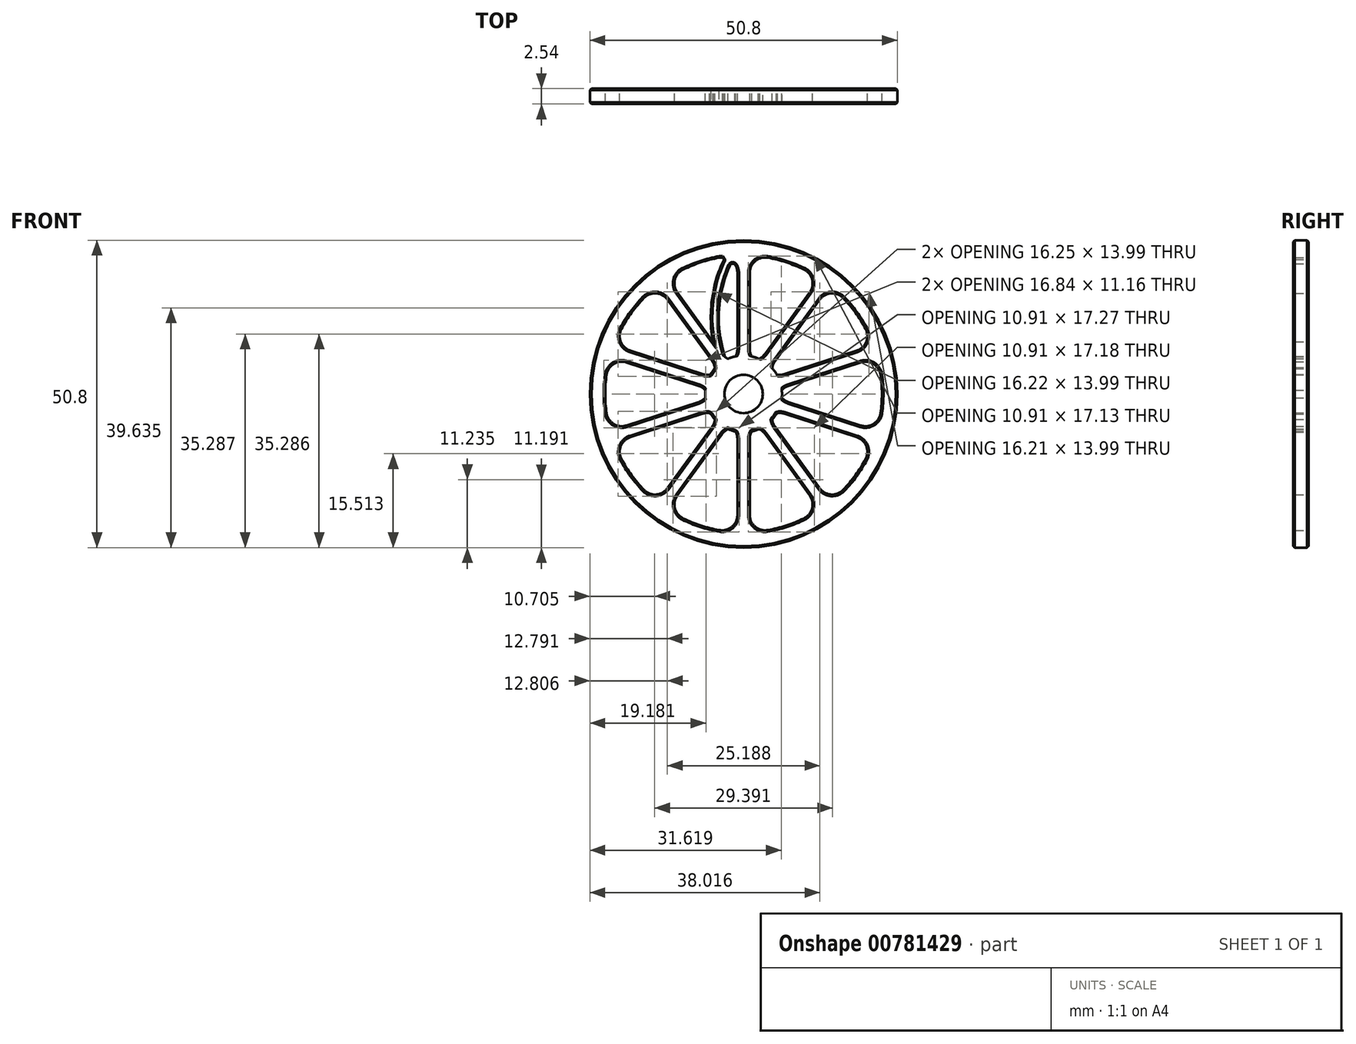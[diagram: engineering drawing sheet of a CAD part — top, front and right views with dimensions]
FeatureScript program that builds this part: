
annotation { "Feature Type Name" : "Feature", "Feature Type Description" : "" }
export const myFeature = defineFeature(function(context is Context, id is Id, definition is map)
    precondition{}
    {
        {
            var Q0;
            Q0=qCreatedBy(makeId("Front.planeOp"),FACE);
            var sketch = newSketch(context, id + "F0", { "sketchPlane" : qUnion([Q0])});
            skCircle(sketch, "E0", {"center": v(0, 0) * mm, "radius": 25.4 * mm});
            skCircle(sketch, "E1", {"center": v(0, 0) * mm, "radius": 3.18 * mm});
            skArc(sketch, "E2", {"start": v(-4, 22.5) * mm, "mid": v(-7.06, 21.74) * mm, "end": v(-10, 20.56) * mm});
            skLineSegment(sketch, "E3", {"start": v(-1.02, 7.45) * mm, "end": v(-1.02, 20) * mm});
            skLineSegment(sketch, "E4.MirrorCS", {"start": v(1.02, 7.45) * mm, "end": v(1.02, 20) * mm});
            skPoint(sketch, "E5.visualSharp", {"position": v(-1.02, 5.62) * mm});
            skArc(sketch, "E5.filletArc", {"start": v(-1.34, 6.2) * mm, "mid": v(-1.1, 6.8) * mm, "end": v(-1.02, 7.45) * mm});
            skPoint(sketch, "E6.visualSharp", {"position": v(1.02, 5.62) * mm});
            skArc(sketch, "E6.filletArc", {"start": v(1.02, 7.45) * mm, "mid": v(1.1, 6.8) * mm, "end": v(1.34, 6.2) * mm});
            skPoint(sketch, "E7.visualSharp", {"position": v(1.02, 22.84) * mm});
            skArc(sketch, "E7.filletArc", {"start": v(4, 22.5) * mm, "mid": v(1.92, 21.95) * mm, "end": v(1.02, 20) * mm});
            skPoint(sketch, "E8.visualSharp", {"position": v(-1.02, 22.84) * mm});
            skArc(sketch, "E8.filletArc", {"start": v(-1.02, 20) * mm, "mid": v(-1.92, 21.95) * mm, "end": v(-4, 22.5) * mm});
            skLineSegment(sketch, "E9.1.0", {"start": v(-5.2, 5.43) * mm, "end": v(-12.58, 15.59) * mm});
            skArc(sketch, "E9.1.1", {"start": v(-12.58, 15.59) * mm, "mid": v(-14.46, 16.63) * mm, "end": v(-16.47, 15.86) * mm});
            skArc(sketch, "E9.1.2", {"start": v(-10, 20.56) * mm, "mid": v(-11.35, 18.9) * mm, "end": v(-10.94, 16.78) * mm});
            skLineSegment(sketch, "E9.1.3", {"start": v(-3.56, 6.62) * mm, "end": v(-10.94, 16.78) * mm});
            skArc(sketch, "E9.1.4", {"start": v(-3.56, 6.62) * mm, "mid": v(-3.11, 6.15) * mm, "end": v(-2.56, 5.8) * mm});
            skArc(sketch, "E9.1.5", {"start": v(-4.73, 4.23) * mm, "mid": v(-4.9, 4.86) * mm, "end": v(-5.2, 5.43) * mm});
            skLineSegment(sketch, "E9.2.0", {"start": v(-7.4, 1.34) * mm, "end": v(-19.34, 5.22) * mm});
            skArc(sketch, "E9.2.1", {"start": v(-19.34, 5.22) * mm, "mid": v(-21.47, 4.95) * mm, "end": v(-22.64, 3.15) * mm});
            skArc(sketch, "E9.2.2", {"start": v(-20.17, 10.76) * mm, "mid": v(-20.28, 8.61) * mm, "end": v(-18.71, 7.15) * mm});
            skLineSegment(sketch, "E9.2.3", {"start": v(-6.77, 3.27) * mm, "end": v(-18.71, 7.15) * mm});
            skArc(sketch, "E9.2.4", {"start": v(-6.77, 3.27) * mm, "mid": v(-6.13, 3.15) * mm, "end": v(-5.49, 3.2) * mm});
            skArc(sketch, "E9.2.5", {"start": v(-6.32, 0.64) * mm, "mid": v(-6.81, 1.06) * mm, "end": v(-7.4, 1.34) * mm});
            skLineSegment(sketch, "E9.3.0", {"start": v(-6.77, -3.27) * mm, "end": v(-18.71, -7.15) * mm});
            skArc(sketch, "E9.3.1", {"start": v(-18.71, -7.15) * mm, "mid": v(-20.28, -8.61) * mm, "end": v(-20.17, -10.76) * mm});
            skArc(sketch, "E9.3.2", {"start": v(-22.64, -3.15) * mm, "mid": v(-21.47, -4.95) * mm, "end": v(-19.34, -5.22) * mm});
            skLineSegment(sketch, "E9.3.3", {"start": v(-7.4, -1.34) * mm, "end": v(-19.34, -5.22) * mm});
            skArc(sketch, "E9.3.4", {"start": v(-7.4, -1.34) * mm, "mid": v(-6.81, -1.06) * mm, "end": v(-6.32, -0.64) * mm});
            skArc(sketch, "E9.3.5", {"start": v(-5.49, -3.2) * mm, "mid": v(-6.13, -3.15) * mm, "end": v(-6.77, -3.27) * mm});
            skLineSegment(sketch, "E9.4.0", {"start": v(-3.56, -6.62) * mm, "end": v(-10.94, -16.78) * mm});
            skArc(sketch, "E9.4.1", {"start": v(-10.94, -16.78) * mm, "mid": v(-11.35, -18.9) * mm, "end": v(-10, -20.56) * mm});
            skArc(sketch, "E9.4.2", {"start": v(-16.47, -15.86) * mm, "mid": v(-14.46, -16.63) * mm, "end": v(-12.58, -15.59) * mm});
            skLineSegment(sketch, "E9.4.3", {"start": v(-5.2, -5.43) * mm, "end": v(-12.58, -15.59) * mm});
            skArc(sketch, "E9.4.4", {"start": v(-5.2, -5.43) * mm, "mid": v(-4.9, -4.86) * mm, "end": v(-4.73, -4.23) * mm});
            skArc(sketch, "E9.4.5", {"start": v(-2.56, -5.8) * mm, "mid": v(-3.11, -6.15) * mm, "end": v(-3.56, -6.62) * mm});
            skLineSegment(sketch, "E9.5.0", {"start": v(1.02, -7.45) * mm, "end": v(1.02, -20) * mm});
            skArc(sketch, "E9.5.1", {"start": v(1.02, -20) * mm, "mid": v(1.92, -21.95) * mm, "end": v(4, -22.5) * mm});
            skArc(sketch, "E9.5.2", {"start": v(-4, -22.5) * mm, "mid": v(-1.92, -21.95) * mm, "end": v(-1.02, -20) * mm});
            skLineSegment(sketch, "E9.5.3", {"start": v(-1.02, -7.45) * mm, "end": v(-1.02, -20) * mm});
            skArc(sketch, "E9.5.4", {"start": v(-1.02, -7.45) * mm, "mid": v(-1.1, -6.8) * mm, "end": v(-1.34, -6.2) * mm});
            skArc(sketch, "E9.5.5", {"start": v(1.34, -6.2) * mm, "mid": v(1.1, -6.8) * mm, "end": v(1.02, -7.45) * mm});
            skLineSegment(sketch, "E9.6.0", {"start": v(5.2, -5.43) * mm, "end": v(12.58, -15.59) * mm});
            skArc(sketch, "E9.6.1", {"start": v(12.58, -15.59) * mm, "mid": v(14.46, -16.63) * mm, "end": v(16.47, -15.86) * mm});
            skArc(sketch, "E9.6.2", {"start": v(10, -20.56) * mm, "mid": v(11.35, -18.9) * mm, "end": v(10.94, -16.78) * mm});
            skLineSegment(sketch, "E9.6.3", {"start": v(3.56, -6.62) * mm, "end": v(10.94, -16.78) * mm});
            skArc(sketch, "E9.6.4", {"start": v(3.56, -6.62) * mm, "mid": v(3.11, -6.15) * mm, "end": v(2.56, -5.8) * mm});
            skArc(sketch, "E9.6.5", {"start": v(4.73, -4.23) * mm, "mid": v(4.9, -4.86) * mm, "end": v(5.2, -5.43) * mm});
            skLineSegment(sketch, "E9.7.0", {"start": v(7.4, -1.34) * mm, "end": v(19.34, -5.22) * mm});
            skArc(sketch, "E9.7.1", {"start": v(19.34, -5.22) * mm, "mid": v(21.47, -4.95) * mm, "end": v(22.64, -3.15) * mm});
            skArc(sketch, "E9.7.2", {"start": v(20.17, -10.76) * mm, "mid": v(20.28, -8.61) * mm, "end": v(18.71, -7.15) * mm});
            skLineSegment(sketch, "E9.7.3", {"start": v(6.77, -3.27) * mm, "end": v(18.71, -7.15) * mm});
            skArc(sketch, "E9.7.4", {"start": v(6.77, -3.27) * mm, "mid": v(6.13, -3.15) * mm, "end": v(5.49, -3.2) * mm});
            skArc(sketch, "E9.7.5", {"start": v(6.32, -0.64) * mm, "mid": v(6.81, -1.06) * mm, "end": v(7.4, -1.34) * mm});
            skLineSegment(sketch, "E9.8.0", {"start": v(6.77, 3.27) * mm, "end": v(18.71, 7.15) * mm});
            skArc(sketch, "E9.8.1", {"start": v(18.71, 7.15) * mm, "mid": v(20.28, 8.61) * mm, "end": v(20.17, 10.76) * mm});
            skArc(sketch, "E9.8.2", {"start": v(22.64, 3.15) * mm, "mid": v(21.47, 4.95) * mm, "end": v(19.34, 5.22) * mm});
            skLineSegment(sketch, "E9.8.3", {"start": v(7.4, 1.34) * mm, "end": v(19.34, 5.22) * mm});
            skArc(sketch, "E9.8.4", {"start": v(7.4, 1.34) * mm, "mid": v(6.81, 1.06) * mm, "end": v(6.32, 0.64) * mm});
            skArc(sketch, "E9.8.5", {"start": v(5.49, 3.2) * mm, "mid": v(6.13, 3.15) * mm, "end": v(6.77, 3.27) * mm});
            skLineSegment(sketch, "E9.9.0", {"start": v(3.56, 6.62) * mm, "end": v(10.94, 16.78) * mm});
            skArc(sketch, "E9.9.1", {"start": v(10.94, 16.78) * mm, "mid": v(11.35, 18.9) * mm, "end": v(10, 20.56) * mm});
            skArc(sketch, "E9.9.2", {"start": v(16.47, 15.86) * mm, "mid": v(14.46, 16.63) * mm, "end": v(12.58, 15.59) * mm});
            skLineSegment(sketch, "E9.9.3", {"start": v(5.2, 5.43) * mm, "end": v(12.58, 15.59) * mm});
            skArc(sketch, "E9.9.4", {"start": v(5.2, 5.43) * mm, "mid": v(4.9, 4.86) * mm, "end": v(4.73, 4.23) * mm});
            skArc(sketch, "E9.9.5", {"start": v(2.56, 5.8) * mm, "mid": v(3.11, 6.15) * mm, "end": v(3.56, 6.62) * mm});
            skArc(sketch, "E10.trimOffspring", {"start": v(-16.47, 15.86) * mm, "mid": v(-18.5, 13.44) * mm, "end": v(-20.17, 10.76) * mm});
            skArc(sketch, "E11.trimOffspring", {"start": v(10, 20.56) * mm, "mid": v(7.06, 21.74) * mm, "end": v(4, 22.5) * mm});
            skArc(sketch, "E12.trimOffspring", {"start": v(20.17, 10.76) * mm, "mid": v(18.5, 13.44) * mm, "end": v(16.47, 15.86) * mm});
            skArc(sketch, "E13.trimOffspring", {"start": v(22.64, -3.15) * mm, "mid": v(22.86, 0) * mm, "end": v(22.64, 3.15) * mm});
            skArc(sketch, "E14.trimOffspring", {"start": v(16.47, -15.86) * mm, "mid": v(18.5, -13.44) * mm, "end": v(20.17, -10.76) * mm});
            skArc(sketch, "E15.trimOffspring", {"start": v(4, -22.5) * mm, "mid": v(7.06, -21.74) * mm, "end": v(10, -20.56) * mm});
            skArc(sketch, "E16.trimOffspring", {"start": v(-10, -20.56) * mm, "mid": v(-7.06, -21.74) * mm, "end": v(-4, -22.5) * mm});
            skArc(sketch, "E17.trimOffspring", {"start": v(-20.17, -10.76) * mm, "mid": v(-18.5, -13.44) * mm, "end": v(-16.47, -15.86) * mm});
            skArc(sketch, "E18.trimOffspring", {"start": v(-22.64, 3.15) * mm, "mid": v(-22.86, 0) * mm, "end": v(-22.64, -3.15) * mm});
            skPoint(sketch, "E19.orphan", {"position": v(-5.67, 0.75) * mm});
            skPoint(sketch, "E20.orphan", {"position": v(-5.67, -0.75) * mm});
            skPoint(sketch, "E21.orphan", {"position": v(-4.14, 3.94) * mm});
            skPoint(sketch, "E22.orphan", {"position": v(-5.02, 2.73) * mm});
            skPoint(sketch, "E23.orphan", {"position": v(-1.04, 5.62) * mm});
            skPoint(sketch, "E24.orphan", {"position": v(1.04, 5.62) * mm});
            skPoint(sketch, "E25.orphan", {"position": v(4.14, 3.94) * mm});
            skPoint(sketch, "E26.orphan", {"position": v(5.02, 2.73) * mm});
            skPoint(sketch, "E27.orphan", {"position": v(5.67, 0.75) * mm});
            skPoint(sketch, "E28.orphan", {"position": v(5.67, -0.75) * mm});
            skPoint(sketch, "E29.orphan", {"position": v(5.02, -2.73) * mm});
            skPoint(sketch, "E30.orphan", {"position": v(4.14, -3.94) * mm});
            skPoint(sketch, "E31.orphan", {"position": v(2.46, -5.16) * mm});
            skPoint(sketch, "E32.orphan", {"position": v(1.04, -5.62) * mm});
            skPoint(sketch, "E33.orphan", {"position": v(-1.04, -5.62) * mm});
            skPoint(sketch, "E34.orphan", {"position": v(-2.46, -5.16) * mm});
            skPoint(sketch, "E35.orphan", {"position": v(-4.14, -3.94) * mm});
            skPoint(sketch, "E36.orphan", {"position": v(-5.02, -2.73) * mm});
            skPoint(sketch, "E37.orphan", {"position": v(-2.46, 5.16) * mm});
            skArc(sketch, "E38", {"start": v(-4.73, 4.23) * mm, "mid": v(-5.14, 3.73) * mm, "end": v(-5.49, 3.2) * mm});
            skArc(sketch, "E39.trimOffspring", {"start": v(-1.34, 6.2) * mm, "mid": v(-1.96, 6.04) * mm, "end": v(-2.56, 5.8) * mm});
            skArc(sketch, "E40.trimOffspring", {"start": v(2.56, 5.8) * mm, "mid": v(1.96, 6.04) * mm, "end": v(1.34, 6.2) * mm});
            skArc(sketch, "E41.trimOffspring", {"start": v(5.49, 3.2) * mm, "mid": v(5.14, 3.73) * mm, "end": v(4.73, 4.23) * mm});
            skArc(sketch, "E42.trimOffspring", {"start": v(6.32, -0.64) * mm, "mid": v(6.35, 0) * mm, "end": v(6.32, 0.64) * mm});
            skArc(sketch, "E43.trimOffspring", {"start": v(-6.32, 0.64) * mm, "mid": v(-6.35, 0) * mm, "end": v(-6.32, -0.64) * mm});
            skArc(sketch, "E44.trimOffspring", {"start": v(-5.49, -3.2) * mm, "mid": v(-5.14, -3.73) * mm, "end": v(-4.73, -4.23) * mm});
            skArc(sketch, "E45.trimOffspring", {"start": v(1.34, -6.2) * mm, "mid": v(1.96, -6.04) * mm, "end": v(2.56, -5.8) * mm});
            skArc(sketch, "E46.trimOffspring", {"start": v(4.73, -4.23) * mm, "mid": v(5.14, -3.73) * mm, "end": v(5.49, -3.2) * mm});
            skArc(sketch, "E47.trimOffspring", {"start": v(-2.56, -5.8) * mm, "mid": v(-1.96, -6.04) * mm, "end": v(-1.34, -6.2) * mm});
            skSolve(sketch);
        }
        {
            var Q0;
            Q0=makeQuery(id+"F0.imprint","IMPRINT",FACE,{"disambiguationData":[TD([[makeQuery(id+"F0.imprint","IMPRINT",EDGE,{"derivedFrom":sQuery(id+"F0.wireOp",EDGE,"E0")}),1.0]])]});
            extrude(context, id + "F1", {"entities" : qUnion([Q0]), "depth" : 2.54 * mm, "offsetDistance" : 25.4 * mm});
        }
        {
            var Q0;
            Q0=makeQuery(id+"F1.opExtrude","CAP_FACE",FACE,{"disambiguationData":[OSD([sQuery(id+"F0.wireOp",EDGE,"E0"),sQuery(id+"F0.wireOp",EDGE,"E1"),sQuery(id+"F0.wireOp",EDGE,"E2"),sQuery(id+"F0.wireOp",EDGE,"E3"),sQuery(id+"F0.wireOp",EDGE,"E4.MirrorCS"),sQuery(id+"F0.wireOp",EDGE,"E5.filletArc"),sQuery(id+"F0.wireOp",EDGE,"E6.filletArc"),sQuery(id+"F0.wireOp",EDGE,"E7.filletArc"),sQuery(id+"F0.wireOp",EDGE,"E8.filletArc"),sQuery(id+"F0.wireOp",EDGE,"E9.1.0"),sQuery(id+"F0.wireOp",EDGE,"E9.1.1"),sQuery(id+"F0.wireOp",EDGE,"E9.1.2"),sQuery(id+"F0.wireOp",EDGE,"E9.1.3"),sQuery(id+"F0.wireOp",EDGE,"E9.1.4"),sQuery(id+"F0.wireOp",EDGE,"E9.1.5"),sQuery(id+"F0.wireOp",EDGE,"E9.2.0"),sQuery(id+"F0.wireOp",EDGE,"E9.2.1"),sQuery(id+"F0.wireOp",EDGE,"E9.2.2"),sQuery(id+"F0.wireOp",EDGE,"E9.2.3"),sQuery(id+"F0.wireOp",EDGE,"E9.2.4"),sQuery(id+"F0.wireOp",EDGE,"E9.2.5"),sQuery(id+"F0.wireOp",EDGE,"E9.3.0"),sQuery(id+"F0.wireOp",EDGE,"E9.3.1"),sQuery(id+"F0.wireOp",EDGE,"E9.3.2"),sQuery(id+"F0.wireOp",EDGE,"E9.3.3"),sQuery(id+"F0.wireOp",EDGE,"E9.3.4"),sQuery(id+"F0.wireOp",EDGE,"E9.3.5"),sQuery(id+"F0.wireOp",EDGE,"E9.4.0"),sQuery(id+"F0.wireOp",EDGE,"E9.4.1"),sQuery(id+"F0.wireOp",EDGE,"E9.4.2"),sQuery(id+"F0.wireOp",EDGE,"E9.4.3"),sQuery(id+"F0.wireOp",EDGE,"E9.4.4"),sQuery(id+"F0.wireOp",EDGE,"E9.4.5"),sQuery(id+"F0.wireOp",EDGE,"E9.5.0"),sQuery(id+"F0.wireOp",EDGE,"E9.5.1"),sQuery(id+"F0.wireOp",EDGE,"E9.5.2"),sQuery(id+"F0.wireOp",EDGE,"E9.5.3"),sQuery(id+"F0.wireOp",EDGE,"E9.5.4"),sQuery(id+"F0.wireOp",EDGE,"E9.5.5"),sQuery(id+"F0.wireOp",EDGE,"E9.6.0"),sQuery(id+"F0.wireOp",EDGE,"E9.6.1"),sQuery(id+"F0.wireOp",EDGE,"E9.6.2"),sQuery(id+"F0.wireOp",EDGE,"E9.6.3"),sQuery(id+"F0.wireOp",EDGE,"E9.6.4"),sQuery(id+"F0.wireOp",EDGE,"E9.6.5"),sQuery(id+"F0.wireOp",EDGE,"E9.7.0"),sQuery(id+"F0.wireOp",EDGE,"E9.7.1"),sQuery(id+"F0.wireOp",EDGE,"E9.7.2"),sQuery(id+"F0.wireOp",EDGE,"E9.7.3"),sQuery(id+"F0.wireOp",EDGE,"E9.7.4"),sQuery(id+"F0.wireOp",EDGE,"E9.7.5"),sQuery(id+"F0.wireOp",EDGE,"E9.8.0"),sQuery(id+"F0.wireOp",EDGE,"E9.8.1"),sQuery(id+"F0.wireOp",EDGE,"E9.8.2"),sQuery(id+"F0.wireOp",EDGE,"E9.8.3"),sQuery(id+"F0.wireOp",EDGE,"E9.8.4"),sQuery(id+"F0.wireOp",EDGE,"E9.8.5"),sQuery(id+"F0.wireOp",EDGE,"E9.9.0"),sQuery(id+"F0.wireOp",EDGE,"E9.9.1"),sQuery(id+"F0.wireOp",EDGE,"E9.9.2"),sQuery(id+"F0.wireOp",EDGE,"E9.9.3"),sQuery(id+"F0.wireOp",EDGE,"E9.9.4"),sQuery(id+"F0.wireOp",EDGE,"E9.9.5"),sQuery(id+"F0.wireOp",EDGE,"E10.trimOffspring"),sQuery(id+"F0.wireOp",EDGE,"E11.trimOffspring"),sQuery(id+"F0.wireOp",EDGE,"E12.trimOffspring"),sQuery(id+"F0.wireOp",EDGE,"E13.trimOffspring"),sQuery(id+"F0.wireOp",EDGE,"E14.trimOffspring"),sQuery(id+"F0.wireOp",EDGE,"E15.trimOffspring"),sQuery(id+"F0.wireOp",EDGE,"E16.trimOffspring"),sQuery(id+"F0.wireOp",EDGE,"E17.trimOffspring"),sQuery(id+"F0.wireOp",EDGE,"E18.trimOffspring"),sQuery(id+"F0.wireOp",EDGE,"E44.trimOffspring"),sQuery(id+"F0.wireOp",EDGE,"E47.trimOffspring"),sQuery(id+"F0.wireOp",EDGE,"E45.trimOffspring"),sQuery(id+"F0.wireOp",EDGE,"E46.trimOffspring"),sQuery(id+"F0.wireOp",EDGE,"E42.trimOffspring"),sQuery(id+"F0.wireOp",EDGE,"E41.trimOffspring"),sQuery(id+"F0.wireOp",EDGE,"E40.trimOffspring"),sQuery(id+"F0.wireOp",EDGE,"E39.trimOffspring"),sQuery(id+"F0.wireOp",EDGE,"E38"),sQuery(id+"F0.wireOp",EDGE,"E43.trimOffspring")])],"isStart":true});
            var sketch = newSketch(context, id + "F2", { "sketchPlane" : qUnion([Q0])});
            skLineSegment(sketch, "E48", {"start": v(1.02, 13.73) * mm, "end": v(7.25, 11.7) * mm, "construction": true});
            skFitSpline(sketch, "E49", {"points": [v(1.92, 21.95) * mm, v(4.13, 12.72) * mm, v(3.11, 6.15) * mm], "startDerivative": vector(8, -16.77) * mm, "endDerivative": vector(-3.67, -13.83) * mm});
            skFitSpline(sketch, "E50.0", {"points": [v(3.07, 22.5) * mm, v(3.78, 21.02) * mm, v(4.59, 18.72) * mm, v(5.2, 15.68) * mm, v(5.38, 13.84) * mm, v(5.41, 12.42) * mm, v(5.36, 11.05) * mm, v(5.17, 9.42) * mm, v(4.8, 7.59) * mm, v(4.5, 6.41) * mm, v(4.34, 5.83) * mm]});
            skLineSegment(sketch, "E51.0", {"start": v(3.56, 6.62) * mm, "end": v(10.94, 16.78) * mm});
            skArc(sketch, "E52.0", {"start": v(3.56, 6.62) * mm, "mid": v(3.11, 6.15) * mm, "end": v(2.56, 5.8) * mm});
            skArc(sketch, "E53.0", {"start": v(1.02, 20) * mm, "mid": v(1.92, 21.95) * mm, "end": v(4, 22.5) * mm});
            skSolve(sketch);
        }
        {
            var Q0;
            {var subQ3=sQuery(id+"F2.wireOp",EDGE,"E49");Q0=makeQuery(id+"F2.imprint","IMPRINT",FACE,{"disambiguationData":[TD([[makeQuery(id+"F2.imprint","IMPRINT",EDGE,{"derivedFrom":subQ3}),1.0]])]});}
            var Q1;
            Q1=makeQuery(id+"F1.opExtrude","CAP_FACE",FACE,{"disambiguationData":[OSD([sQuery(id+"F0.wireOp",EDGE,"E0"),sQuery(id+"F0.wireOp",EDGE,"E1"),sQuery(id+"F0.wireOp",EDGE,"E2"),sQuery(id+"F0.wireOp",EDGE,"E3"),sQuery(id+"F0.wireOp",EDGE,"E4.MirrorCS"),sQuery(id+"F0.wireOp",EDGE,"E5.filletArc"),sQuery(id+"F0.wireOp",EDGE,"E6.filletArc"),sQuery(id+"F0.wireOp",EDGE,"E7.filletArc"),sQuery(id+"F0.wireOp",EDGE,"E8.filletArc"),sQuery(id+"F0.wireOp",EDGE,"E9.1.0"),sQuery(id+"F0.wireOp",EDGE,"E9.1.1"),sQuery(id+"F0.wireOp",EDGE,"E9.1.2"),sQuery(id+"F0.wireOp",EDGE,"E9.1.3"),sQuery(id+"F0.wireOp",EDGE,"E9.1.4"),sQuery(id+"F0.wireOp",EDGE,"E9.1.5"),sQuery(id+"F0.wireOp",EDGE,"E9.2.0"),sQuery(id+"F0.wireOp",EDGE,"E9.2.1"),sQuery(id+"F0.wireOp",EDGE,"E9.2.2"),sQuery(id+"F0.wireOp",EDGE,"E9.2.3"),sQuery(id+"F0.wireOp",EDGE,"E9.2.4"),sQuery(id+"F0.wireOp",EDGE,"E9.2.5"),sQuery(id+"F0.wireOp",EDGE,"E9.3.0"),sQuery(id+"F0.wireOp",EDGE,"E9.3.1"),sQuery(id+"F0.wireOp",EDGE,"E9.3.2"),sQuery(id+"F0.wireOp",EDGE,"E9.3.3"),sQuery(id+"F0.wireOp",EDGE,"E9.3.4"),sQuery(id+"F0.wireOp",EDGE,"E9.3.5"),sQuery(id+"F0.wireOp",EDGE,"E9.4.0"),sQuery(id+"F0.wireOp",EDGE,"E9.4.1"),sQuery(id+"F0.wireOp",EDGE,"E9.4.2"),sQuery(id+"F0.wireOp",EDGE,"E9.4.3"),sQuery(id+"F0.wireOp",EDGE,"E9.4.4"),sQuery(id+"F0.wireOp",EDGE,"E9.4.5"),sQuery(id+"F0.wireOp",EDGE,"E9.5.0"),sQuery(id+"F0.wireOp",EDGE,"E9.5.1"),sQuery(id+"F0.wireOp",EDGE,"E9.5.2"),sQuery(id+"F0.wireOp",EDGE,"E9.5.3"),sQuery(id+"F0.wireOp",EDGE,"E9.5.4"),sQuery(id+"F0.wireOp",EDGE,"E9.5.5"),sQuery(id+"F0.wireOp",EDGE,"E9.6.0"),sQuery(id+"F0.wireOp",EDGE,"E9.6.1"),sQuery(id+"F0.wireOp",EDGE,"E9.6.2"),sQuery(id+"F0.wireOp",EDGE,"E9.6.3"),sQuery(id+"F0.wireOp",EDGE,"E9.6.4"),sQuery(id+"F0.wireOp",EDGE,"E9.6.5"),sQuery(id+"F0.wireOp",EDGE,"E9.7.0"),sQuery(id+"F0.wireOp",EDGE,"E9.7.1"),sQuery(id+"F0.wireOp",EDGE,"E9.7.2"),sQuery(id+"F0.wireOp",EDGE,"E9.7.3"),sQuery(id+"F0.wireOp",EDGE,"E9.7.4"),sQuery(id+"F0.wireOp",EDGE,"E9.7.5"),sQuery(id+"F0.wireOp",EDGE,"E9.8.0"),sQuery(id+"F0.wireOp",EDGE,"E9.8.1"),sQuery(id+"F0.wireOp",EDGE,"E9.8.2"),sQuery(id+"F0.wireOp",EDGE,"E9.8.3"),sQuery(id+"F0.wireOp",EDGE,"E9.8.4"),sQuery(id+"F0.wireOp",EDGE,"E9.8.5"),sQuery(id+"F0.wireOp",EDGE,"E9.9.0"),sQuery(id+"F0.wireOp",EDGE,"E9.9.1"),sQuery(id+"F0.wireOp",EDGE,"E9.9.2"),sQuery(id+"F0.wireOp",EDGE,"E9.9.3"),sQuery(id+"F0.wireOp",EDGE,"E9.9.4"),sQuery(id+"F0.wireOp",EDGE,"E9.9.5"),sQuery(id+"F0.wireOp",EDGE,"E10.trimOffspring"),sQuery(id+"F0.wireOp",EDGE,"E11.trimOffspring"),sQuery(id+"F0.wireOp",EDGE,"E12.trimOffspring"),sQuery(id+"F0.wireOp",EDGE,"E13.trimOffspring"),sQuery(id+"F0.wireOp",EDGE,"E14.trimOffspring"),sQuery(id+"F0.wireOp",EDGE,"E15.trimOffspring"),sQuery(id+"F0.wireOp",EDGE,"E16.trimOffspring"),sQuery(id+"F0.wireOp",EDGE,"E17.trimOffspring"),sQuery(id+"F0.wireOp",EDGE,"E18.trimOffspring"),sQuery(id+"F0.wireOp",EDGE,"E44.trimOffspring"),sQuery(id+"F0.wireOp",EDGE,"E47.trimOffspring"),sQuery(id+"F0.wireOp",EDGE,"E45.trimOffspring"),sQuery(id+"F0.wireOp",EDGE,"E46.trimOffspring"),sQuery(id+"F0.wireOp",EDGE,"E42.trimOffspring"),sQuery(id+"F0.wireOp",EDGE,"E41.trimOffspring"),sQuery(id+"F0.wireOp",EDGE,"E40.trimOffspring"),sQuery(id+"F0.wireOp",EDGE,"E39.trimOffspring"),sQuery(id+"F0.wireOp",EDGE,"E38"),sQuery(id+"F0.wireOp",EDGE,"E43.trimOffspring")])],"isStart":false});
            extrude(context, id + "F3", {"entities" : qUnion([Q0]), "operationType" : NewBodyOperationType.ADD, "endBound" : BoundingType.UP_TO_SURFACE, "oppositeDirection" : true, "depth" : 25.4 * mm, "endBoundEntityFace" : qUnion([Q1]), "offsetDistance" : 25.4 * mm});
        }
        {
            var Q0;
            Q0=makeQuery(id+"F3.opExtrude","SWEPT_EDGE",EDGE,{"disambiguationData":[OSD([sQuery(id+"F2.wireOp",EDGE,"E49"),sQuery(id+"F2.wireOp",EDGE,"E53.0")])]});
            var Q1;
            Q1=makeQuery(id+"F3.opExtrude","SWEPT_EDGE",EDGE,{"disambiguationData":[OSD([sQuery(id+"F2.wireOp",EDGE,"E50.0"),sQuery(id+"F2.wireOp",EDGE,"E53.0")])]});
            var Q2;
            Q2=makeQuery(id+"F3.opExtrude","SWEPT_EDGE",EDGE,{"disambiguationData":[OSD([sQuery(id+"F2.wireOp",EDGE,"E50.0"),sQuery(id+"F2.wireOp",EDGE,"E51.0")])]});
            var Q3;
            Q3=makeQuery(id+"F3.opExtrude","SWEPT_EDGE",EDGE,{"disambiguationData":[OSD([sQuery(id+"F2.wireOp",EDGE,"E49"),sQuery(id+"F2.wireOp",EDGE,"E52.0")])]});
            var Q4;
            Q4=makeQuery(id+"Fvi5l6d25C6B4QC_1.1.F3.opExtrude","SWEPT_EDGE",EDGE,{"disambiguationData":[OSD([sQuery(id+"F2.wireOp",EDGE,"E50.0"),sQuery(id+"F2.wireOp",EDGE,"E53.0")])]});
            var Q5;
            Q5=makeQuery(id+"Fvi5l6d25C6B4QC_1.2.F3.opExtrude","SWEPT_EDGE",EDGE,{"disambiguationData":[OSD([sQuery(id+"F2.wireOp",EDGE,"E50.0"),sQuery(id+"F2.wireOp",EDGE,"E53.0")])]});
            var Q6;
            Q6=makeQuery(id+"Fvi5l6d25C6B4QC_1.1.F3.opExtrude","SWEPT_EDGE",EDGE,{"disambiguationData":[OSD([sQuery(id+"F2.wireOp",EDGE,"E49"),sQuery(id+"F2.wireOp",EDGE,"E53.0")])]});
            var Q7;
            Q7=makeQuery(id+"Fvi5l6d25C6B4QC_1.2.F3.opExtrude","SWEPT_EDGE",EDGE,{"disambiguationData":[OSD([sQuery(id+"F2.wireOp",EDGE,"E49"),sQuery(id+"F2.wireOp",EDGE,"E53.0")])]});
            var Q8;
            Q8=makeQuery(id+"Fvi5l6d25C6B4QC_1.1.F3.opExtrude","SWEPT_EDGE",EDGE,{"disambiguationData":[OSD([sQuery(id+"F2.wireOp",EDGE,"E50.0"),sQuery(id+"F2.wireOp",EDGE,"E51.0")])]});
            var Q9;
            Q9=makeQuery(id+"Fvi5l6d25C6B4QC_1.2.F3.opExtrude","SWEPT_EDGE",EDGE,{"disambiguationData":[OSD([sQuery(id+"F2.wireOp",EDGE,"E49"),sQuery(id+"F2.wireOp",EDGE,"E52.0")])]});
            var Q10;
            Q10=makeQuery(id+"Fvi5l6d25C6B4QC_1.1.F3.opExtrude","SWEPT_EDGE",EDGE,{"disambiguationData":[OSD([sQuery(id+"F2.wireOp",EDGE,"E49"),sQuery(id+"F2.wireOp",EDGE,"E52.0")])]});
            var Q11;
            Q11=makeQuery(id+"Fvi5l6d25C6B4QC_1.2.F3.opExtrude","SWEPT_EDGE",EDGE,{"disambiguationData":[OSD([sQuery(id+"F2.wireOp",EDGE,"E50.0"),sQuery(id+"F2.wireOp",EDGE,"E51.0")])]});
            fillet(context, id + "F4", {"entities" : qUnion([Q0, Q1, Q2, Q3, Q4, Q5, Q6, Q7, Q8, Q9, Q10, Q11]), "radius" : 0.5 * mm, "tangentPropagation" : true, "allowEdgeOverflow" : false});
        }
        {
            var Q0;
            Q0=makeQuery(id+"F1.opExtrude","CAP_EDGE",EDGE,{"disambiguationData":[OSD([sQuery(id+"F0.wireOp",EDGE,"E7.filletArc")])],"isStart":false});
            var Q1;
            Q1=makeQuery(id+"F1.opExtrude","CAP_EDGE",EDGE,{"disambiguationData":[OSD([sQuery(id+"F0.wireOp",EDGE,"E9.9.2")])],"isStart":false});
            var Q2;
            Q2=makeQuery(id+"F1.opExtrude","SWEPT_FACE",FACE,{"disambiguationData":[OSD([sQuery(id+"F0.wireOp",EDGE,"E9.8.2")])]});
            var Q3;
            Q3=makeQuery(id+"F1.opExtrude","SWEPT_FACE",FACE,{"disambiguationData":[OSD([sQuery(id+"F0.wireOp",EDGE,"E12.trimOffspring")])]});
            var Q4;
            Q4=makeQuery(id+"F1.opExtrude","SWEPT_FACE",FACE,{"disambiguationData":[OSD([sQuery(id+"F0.wireOp",EDGE,"E11.trimOffspring")])]});
            var Q5;
            Q5=makeQuery(id+"F1.opExtrude","SWEPT_FACE",FACE,{"disambiguationData":[OSD([sQuery(id+"F0.wireOp",EDGE,"E8.filletArc")])]});
            var Q6;
            Q6=makeQuery(id+"F1.opExtrude","SWEPT_FACE",FACE,{"disambiguationData":[OSD([sQuery(id+"F0.wireOp",EDGE,"E9.1.0")])]});
            var Q7;
            Q7=makeQuery(id+"F1.opExtrude","SWEPT_FACE",FACE,{"disambiguationData":[OSD([sQuery(id+"F0.wireOp",EDGE,"E9.2.0")])]});
            var Q8;
            Q8=makeQuery(id+"F1.opExtrude","SWEPT_FACE",FACE,{"disambiguationData":[OSD([sQuery(id+"F0.wireOp",EDGE,"E9.3.5")])]});
            var Q9;
            Q9=makeQuery(id+"F1.opExtrude","SWEPT_FACE",FACE,{"disambiguationData":[OSD([sQuery(id+"F0.wireOp",EDGE,"E9.5.4")])]});
            var Q10;
            Q10=makeQuery(id+"F1.opExtrude","SWEPT_FACE",FACE,{"disambiguationData":[OSD([sQuery(id+"F0.wireOp",EDGE,"E9.6.4")])]});
            var Q11;
            Q11=makeQuery(id+"F1.opExtrude","SWEPT_FACE",FACE,{"disambiguationData":[OSD([sQuery(id+"F0.wireOp",EDGE,"E9.7.4")])]});
            var Q12;
            Q12=makeQuery(id+"F1.opExtrude","SWEPT_FACE",FACE,{"disambiguationData":[OSD([sQuery(id+"F0.wireOp",EDGE,"E0")])]});
            var Q13;
            Q13=makeQuery(id+"F1.opExtrude","SWEPT_FACE",FACE,{"disambiguationData":[OSD([sQuery(id+"F0.wireOp",EDGE,"E40.trimOffspring")])]});
            var Q14;
            Q14=makeQuery(id+"F1.opExtrude","SWEPT_FACE",FACE,{"disambiguationData":[OSD([sQuery(id+"F0.wireOp",EDGE,"E41.trimOffspring")])]});
            var Q15;
            Q15=makeQuery(id+"F1.opExtrude","SWEPT_FACE",FACE,{"disambiguationData":[OSD([sQuery(id+"F0.wireOp",EDGE,"E39.trimOffspring")])]});
            var Q16;
            Q16=makeQuery(id+"F1.opExtrude","SWEPT_FACE",FACE,{"disambiguationData":[OSD([sQuery(id+"F0.wireOp",EDGE,"E42.trimOffspring")])]});
            var Q17;
            Q17=makeQuery(id+"F1.opExtrude","SWEPT_FACE",FACE,{"disambiguationData":[OSD([sQuery(id+"F0.wireOp",EDGE,"E43.trimOffspring")])]});
            var Q18;
            Q18=makeQuery(id+"F1.opExtrude","SWEPT_EDGE",EDGE,{"disambiguationData":[OSD([sQuery(id+"F0.wireOp",EDGE,"E9.1.5"),sQuery(id+"F0.wireOp",EDGE,"E38")])]});
            var Q19;
            Q19=makeQuery(id+"F1.opExtrude","SWEPT_FACE",FACE,{"disambiguationData":[OSD([sQuery(id+"F0.wireOp",EDGE,"E10.trimOffspring")])]});
            var Q20;
            Q20=makeQuery(id+"Fvi5l6d25C6B4QC_1.3.F3.opExtrude","SWEPT_FACE",FACE,{"disambiguationData":[OSD([sQuery(id+"F2.wireOp",EDGE,"E50.0")])]});
            var Q21;
            Q21=makeQuery(id+"Fvi5l6d25C6B4QC_1.2.F3.opExtrude","SWEPT_FACE",FACE,{"disambiguationData":[OSD([sQuery(id+"F2.wireOp",EDGE,"E50.0")])]});
            var Q22;
            Q22=makeQuery(id+"Fvi5l6d25C6B4QC_1.4.F3.opExtrude","SWEPT_FACE",FACE,{"disambiguationData":[OSD([sQuery(id+"F2.wireOp",EDGE,"E50.0")])]});
            var Q23;
            Q23=makeQuery(id+"Fvi5l6d25C6B4QC_1.5.F3.opExtrude","SWEPT_FACE",FACE,{"disambiguationData":[OSD([sQuery(id+"F2.wireOp",EDGE,"E50.0")])]});
            var Q24;
            Q24=makeQuery(id+"F1.opExtrude","SWEPT_FACE",FACE,{"disambiguationData":[OSD([sQuery(id+"F0.wireOp",EDGE,"E9.7.3")])]});
            chamfer(context, id + "F5", {"entities" : qUnion([Q0, Q1, Q2, Q3, Q4, Q5, Q6, Q7, Q8, Q9, Q10, Q11, Q12, Q13, Q14, Q15, Q16, Q17, Q18, Q19, Q20, Q21, Q22, Q23, Q24]), "width" : 0.25 * mm, "tangentPropagation" : true});
        }
    });
